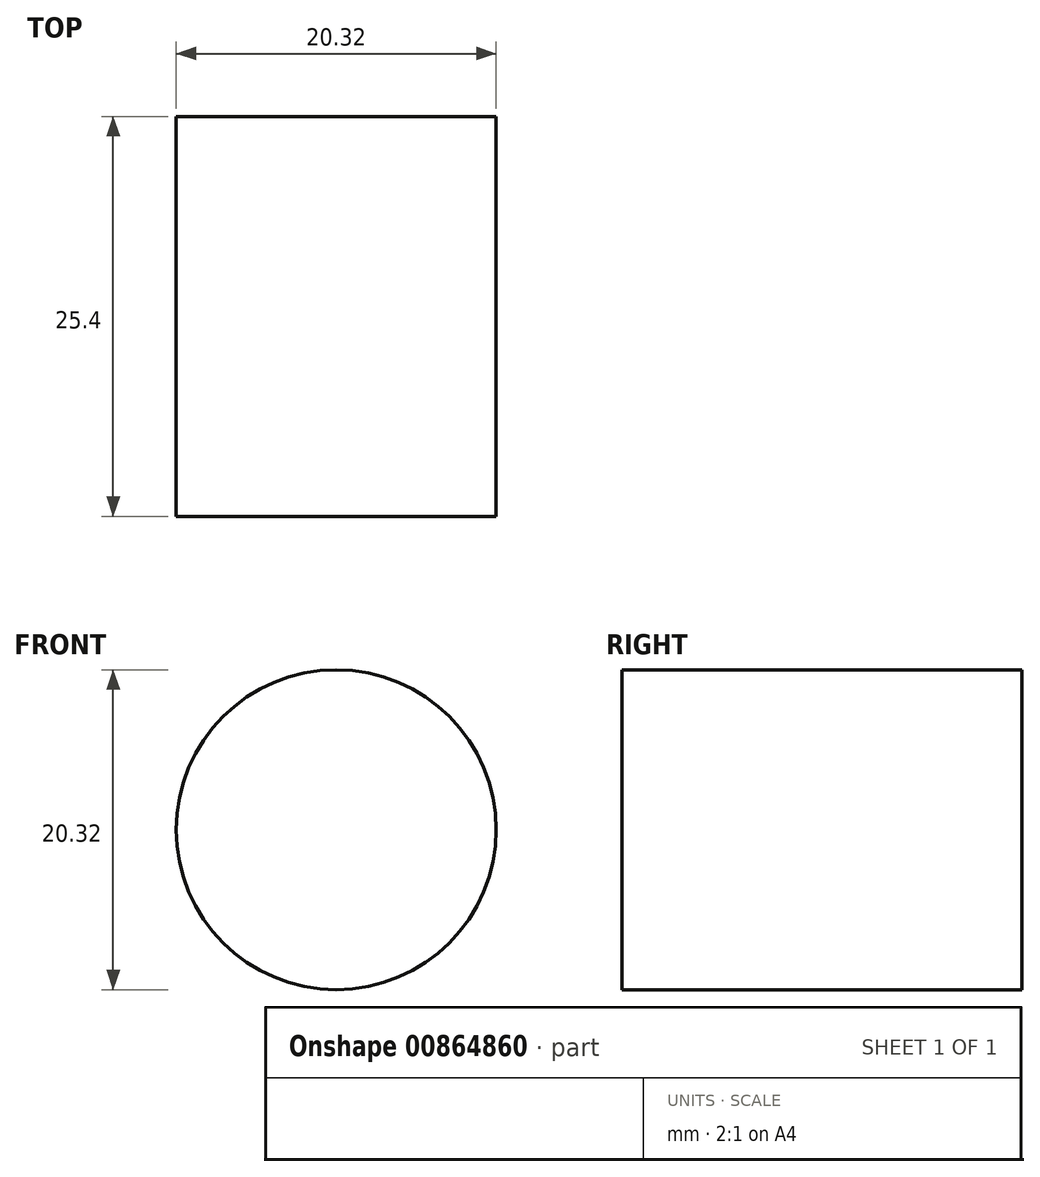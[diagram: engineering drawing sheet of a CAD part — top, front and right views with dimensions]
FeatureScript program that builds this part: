
annotation { "Feature Type Name" : "Feature", "Feature Type Description" : "" }
export const myFeature = defineFeature(function(context is Context, id is Id, definition is map)
    precondition{}
    {
        {
            var Q0;
            Q0=qCreatedBy(makeId("Front.planeOp"),FACE);
            var sketch = newSketch(context, id + "F0", { "sketchPlane" : qUnion([Q0])});
            skCircle(sketch, "E0", {"center": v(0, 0) * mm, "radius": 10.16 * mm});
            skSolve(sketch);
        }
        {
            var Q0;
            Q0=makeQuery(id+"F0.imprint","IMPRINT",FACE,{"disambiguationData":[TD([[makeQuery(id+"F0.imprint","IMPRINT",EDGE,{"derivedFrom":sQuery(id+"F0.wireOp",EDGE,"E0")}),1.0]])]});
            var Q1;
            Q1=sQuery(id+"F0.wireOp",EDGE,"E0");
            extrude(context, id + "F1", {"entities" : qUnion([Q0]), "surfaceOperationType" : NewSurfaceOperationType.ADD, "surfaceEntities" : qUnion([Q1]), "depth" : 25.4 * mm, "offsetDistance" : 25.4 * mm});
        }
    });
